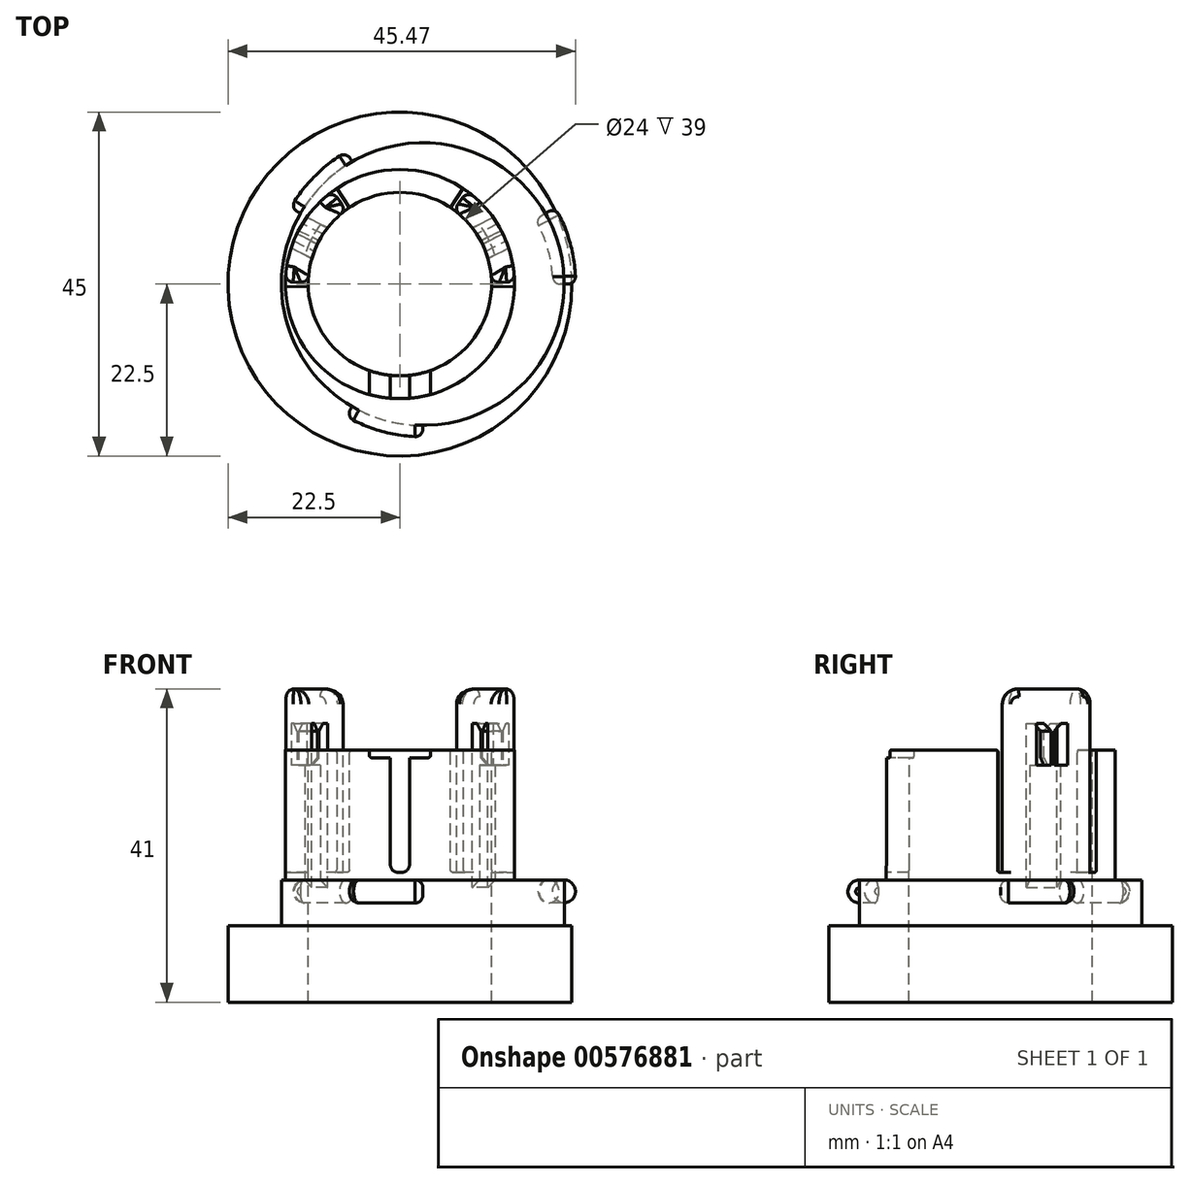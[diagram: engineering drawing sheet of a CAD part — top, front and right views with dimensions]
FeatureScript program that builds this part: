
annotation { "Feature Type Name" : "Feature", "Feature Type Description" : "" }
export const myFeature = defineFeature(function(context is Context, id is Id, definition is map)
    precondition{}
    {
        {
            var Q0;
            Q0=qCreatedBy(makeId("Top.planeOp"),FACE);
            var sketch = newSketch(context, id + "F0", { "sketchPlane" : qUnion([Q0])});
            skCircle(sketch, "E0", {"center": v(0, 0) * mm, "radius": 22.5 * mm});
            skCircle(sketch, "E1", {"center": v(0, 0) * mm, "radius": 12 * mm});
            skSolve(sketch);
        }
        {
            var Q0;
            Q0=makeQuery(id+"F0.imprint","IMPRINT",FACE,{"disambiguationData":[TD([[makeQuery(id+"F0.imprint","IMPRINT",EDGE,{"derivedFrom":sQuery(id+"F0.wireOp",EDGE,"E0")}),1.0]])]});
            extrude(context, id + "F1", {"entities" : qUnion([Q0]), "oppositeDirection" : true, "depth" : 5 * mm, "offsetDistance" : 25 * mm, "hasSecondDirection" : true, "secondDirectionOppositeDirection" : false, "secondDirectionDepth" : 5 * mm});
        }
        {
            var Q0;
            Q0=qCreatedBy(makeId("Top.planeOp"),FACE);
            var sketch = newSketch(context, id + "F2", { "sketchPlane" : qUnion([Q0])});
            skCircle(sketch, "E2", {"center": v(0, 0) * mm, "radius": 12 * mm});
            skCircle(sketch, "E3", {"center": v(3, 0) * mm, "radius": 18.5 * mm});
            skSolve(sketch);
        }
        {
            var Q0;
            Q0 = qSketchRegion(id + "F2", true);
            extrude(context, id + "F3", {"entities" : qUnion([Q0]), "operationType" : NewBodyOperationType.ADD, "depth" : 11 * mm, "offsetDistance" : 25 * mm});
        }
        {
            var Q0;
            Q0=qCreatedBy(makeId("Top.planeOp"),FACE);
            var sketch = newSketch(context, id + "F4", { "sketchPlane" : qUnion([Q0])});
            skCircle(sketch, "E4", {"center": v(0, 0) * mm, "radius": 12 * mm});
            skCircle(sketch, "E5", {"center": v(0, 0) * mm, "radius": 15 * mm});
            skSolve(sketch);
        }
        {
            var Q0;
            Q0 = qSketchRegion(id + "F4", true);
            extrude(context, id + "F5", {"entities" : qUnion([Q0]), "operationType" : NewBodyOperationType.ADD, "depth" : 28 * mm, "offsetDistance" : 25 * mm});
        }
        {
            var Q0;
            Q0=qCreatedBy(makeId("Front.planeOp"),FACE);
            var sketch = newSketch(context, id + "F6", { "sketchPlane" : qUnion([Q0])});
            skCircle(sketch, "E6", {"center": v(21.5, 9.5) * mm, "radius": 1.5 * mm});
            skLineSegment(sketch, "E7", {"start": v(3, -7.37) * mm, "end": v(3, 20.39) * mm});
            skSolve(sketch);
        }
        {
            var Q0;
            Q0=makeQuery(id+"F6.imprint","IMPRINT",FACE,{"disambiguationData":[TD([[makeQuery(id+"F6.imprint","IMPRINT",EDGE,{"derivedFrom":sQuery(id+"F6.wireOp",EDGE,"E6")}),1.0]])]});
            var Q1;
            Q1=sQuery(id+"F6.wireOp",EDGE,"E7");
            revolve(context, id + "F7", {"entities" : qUnion([Q0]), "axis" : qUnion([Q1]), "revolveType" : RevolveType.ONE_DIRECTION, "angle" : 30 * degree});
        }
        {
            var Q0;
            Q0 = qSketchRegion(id + "F6", true);
            var Q1;
            Q1=sQuery(id+"F6.wireOp",EDGE,"E7");
            revolve(context, id + "F8", {"operationType" : NewBodyOperationType.ADD, "entities" : qUnion([Q0]), "axis" : qUnion([Q1]), "revolveType" : RevolveType.TWO_DIRECTIONS, "angle" : 150 * degree, "angleBack" : 120 * degree});
        }
        {
            var Q0;
            Q0 = qSketchRegion(id + "F6", true);
            var Q1;
            Q1=sQuery(id+"F6.wireOp",EDGE,"E7");
            revolve(context, id + "F9", {"operationType" : NewBodyOperationType.ADD, "entities" : qUnion([Q0]), "axis" : qUnion([Q1]), "revolveType" : RevolveType.TWO_DIRECTIONS, "angle" : 270 * degree, "angleBack" : 240 * degree});
        }
        {
            var Q0;
            Q0=makeQuery(id+"F9.opRevolve","CAP_EDGE",EDGE,{"disambiguationData":[OSD([sQuery(id+"F6.wireOp",EDGE,"E6")])],"isStart":false});
            var Q1;
            Q1=makeQuery(id+"F9.opRevolve","CAP_EDGE",EDGE,{"disambiguationData":[OSD([sQuery(id+"F6.wireOp",EDGE,"E6")])],"isStart":true});
            var Q2;
            Q2=makeQuery(id+"F7.opRevolve","CAP_EDGE",EDGE,{"disambiguationData":[OSD([sQuery(id+"F6.wireOp",EDGE,"E6")])],"isStart":true});
            var Q3;
            Q3=makeQuery(id+"F7.opRevolve","CAP_EDGE",EDGE,{"disambiguationData":[OSD([sQuery(id+"F6.wireOp",EDGE,"E6")])],"isStart":false});
            var Q4;
            Q4=makeQuery(id+"F8.opRevolve","CAP_EDGE",EDGE,{"disambiguationData":[OSD([sQuery(id+"F6.wireOp",EDGE,"E6")])],"isStart":true});
            var Q5;
            Q5=makeQuery(id+"F8.opRevolve","CAP_EDGE",EDGE,{"disambiguationData":[OSD([sQuery(id+"F6.wireOp",EDGE,"E6")])],"isStart":false});
            fillet(context, id + "F10", {"entities" : qUnion([Q0, Q1, Q2, Q3, Q4, Q5]), "radius" : 1 * mm, "tangentPropagation" : true, "allowEdgeOverflow" : false});
        }
        {
            var Q0;
            Q0=qCreatedBy(makeId("Top.planeOp"),FACE);
            var sketch = newSketch(context, id + "F11", { "sketchPlane" : qUnion([Q0])});
            skLineSegment(sketch, "E8.bottom", {"start": v(-1.25, -10) * mm, "end": v(1.25, -10) * mm});
            skLineSegment(sketch, "E8.left", {"start": v(-1.25, -10) * mm, "end": v(-1.25, -14.95) * mm});
            skLineSegment(sketch, "E8.right", {"start": v(1.25, -10) * mm, "end": v(1.25, -14.95) * mm});
            skArc(sketch, "E9", {"start": v(-1.25, -14.95) * mm, "mid": v(0, -15) * mm, "end": v(1.25, -14.95) * mm});
            skLineSegment(sketch, "E10", {"start": v(0, 0) * mm, "end": v(-15, -0.4) * mm});
            skLineSegment(sketch, "E11", {"start": v(0, 0) * mm, "end": v(-8.28, 12.5) * mm});
            skLineSegment(sketch, "E12", {"start": v(0, 0) * mm, "end": v(8.28, 12.5) * mm});
            skLineSegment(sketch, "E13", {"start": v(0, 0) * mm, "end": v(15, -0.4) * mm});
            skArc(sketch, "E14.trimOffspring", {"start": v(-8.28, 12.5) * mm, "mid": v(-13.3, 6.93) * mm, "end": v(-15, -0.4) * mm});
            skArc(sketch, "E15.trimOffspring", {"start": v(15, -0.4) * mm, "mid": v(13.3, 6.93) * mm, "end": v(8.28, 12.5) * mm});
            skSolve(sketch);
        }
        {
            var Q0;
            Q0 = qSketchRegion(id + "F11", true);
            extrude(context, id + "F12", {"entities" : qUnion([Q0]), "operationType" : NewBodyOperationType.REMOVE, "depth" : 32 * mm, "offsetDistance" : 25 * mm, "hasSecondDirection" : true, "secondDirectionOppositeDirection" : false, "secondDirectionDepth" : 12 * mm});
        }
        {
            var Q0;
            Q0=makeQuery(id+"F12.boolean.opBoolean","COPY",EDGE,{"derivedFrom":makeQuery(id+"F12.opExtrude","CAP_EDGE",EDGE,{"disambiguationData":[OSD([sQuery(id+"F11.wireOp",EDGE,"E8.left")])],"isStart":true})});
            var Q1;
            Q1=makeQuery(id+"F12.boolean.opBoolean","COPY",EDGE,{"derivedFrom":makeQuery(id+"F12.opExtrude","CAP_EDGE",EDGE,{"disambiguationData":[OSD([sQuery(id+"F11.wireOp",EDGE,"E8.right")])],"isStart":true})});
            fillet(context, id + "F13", {"entities" : qUnion([Q0, Q1]), "radius" : 1 * mm, "tangentPropagation" : true, "allowEdgeOverflow" : false});
        }
        {
            var Q0;
            Q0=qCreatedBy(makeId("Top.planeOp"),FACE);
            var sketch = newSketch(context, id + "F14", { "sketchPlane" : qUnion([Q0])});
            skArc(sketch, "E16", {"start": v(-8.82, 12.14) * mm, "mid": v(-13.3, 6.93) * mm, "end": v(-15, 0.26) * mm});
            skArc(sketch, "E17", {"start": v(-7.05, 9.7) * mm, "mid": v(-10.64, 5.54) * mm, "end": v(-12, 0.2) * mm});
            skLineSegment(sketch, "E18", {"start": v(-12, 0.2) * mm, "end": v(-15, 0.26) * mm});
            skLineSegment(sketch, "E19", {"start": v(-7.05, 9.7) * mm, "end": v(-8.82, 12.14) * mm});
            skLineSegment(sketch, "E20", {"start": v(7.05, 9.7) * mm, "end": v(8.82, 12.14) * mm});
            skLineSegment(sketch, "E21", {"start": v(12, 0.2) * mm, "end": v(15, 0.26) * mm});
            skArc(sketch, "E22.trimOffspring", {"start": v(15, 0.26) * mm, "mid": v(13.3, 6.93) * mm, "end": v(8.82, 12.14) * mm});
            skArc(sketch, "E23.trimOffspring", {"start": v(12, 0.2) * mm, "mid": v(10.64, 5.54) * mm, "end": v(7.05, 9.7) * mm});
            skSolve(sketch);
        }
        {
            var Q0;
            Q0 = qSketchRegion(id + "F14", true);
            extrude(context, id + "F15", {"entities" : qUnion([Q0]), "operationType" : NewBodyOperationType.ADD, "depth" : 36 * mm, "offsetDistance" : 25 * mm, "hasSecondDirection" : true, "secondDirectionOppositeDirection" : false, "secondDirectionDepth" : 11 * mm});
        }
        {
            var Q0;
            Q0=makeQuery(id+"F15.opExtrude","SWEPT_EDGE",EDGE,{"disambiguationData":[OSD([sQuery(id+"F14.wireOp",EDGE,"E16"),sQuery(id+"F14.wireOp",EDGE,"E18")])]});
            var Q1;
            Q1=makeQuery(id+"F15.opExtrude","SWEPT_EDGE",EDGE,{"disambiguationData":[OSD([sQuery(id+"F14.wireOp",EDGE,"E16"),sQuery(id+"F14.wireOp",EDGE,"E19")])]});
            var Q2;
            Q2=makeQuery(id+"F15.opExtrude","SWEPT_EDGE",EDGE,{"disambiguationData":[OSD([sQuery(id+"F14.wireOp",EDGE,"E17"),sQuery(id+"F14.wireOp",EDGE,"E18")])]});
            var Q3;
            Q3=makeQuery(id+"F15.opExtrude","SWEPT_EDGE",EDGE,{"disambiguationData":[OSD([sQuery(id+"F14.wireOp",EDGE,"E17"),sQuery(id+"F14.wireOp",EDGE,"E19")])]});
            var Q4;
            Q4=makeQuery(id+"F15.opExtrude","CAP_EDGE",EDGE,{"disambiguationData":[OSD([sQuery(id+"F14.wireOp",EDGE,"E16")])],"isStart":false});
            var Q5;
            Q5=makeQuery(id+"F15.opExtrude","SWEPT_EDGE",EDGE,{"disambiguationData":[OSD([sQuery(id+"F14.wireOp",EDGE,"E20"),sQuery(id+"F14.wireOp",EDGE,"E23.trimOffspring")])]});
            var Q6;
            Q6=makeQuery(id+"F15.opExtrude","SWEPT_EDGE",EDGE,{"disambiguationData":[OSD([sQuery(id+"F14.wireOp",EDGE,"E21"),sQuery(id+"F14.wireOp",EDGE,"E23.trimOffspring")])]});
            var Q7;
            Q7=makeQuery(id+"F15.opExtrude","SWEPT_EDGE",EDGE,{"disambiguationData":[OSD([sQuery(id+"F14.wireOp",EDGE,"E21"),sQuery(id+"F14.wireOp",EDGE,"E22.trimOffspring")])]});
            var Q8;
            Q8=makeQuery(id+"F15.opExtrude","CAP_EDGE",EDGE,{"disambiguationData":[OSD([sQuery(id+"F14.wireOp",EDGE,"E22.trimOffspring")])],"isStart":false});
            var Q9;
            Q9=makeQuery(id+"F15.opExtrude","SWEPT_EDGE",EDGE,{"disambiguationData":[OSD([sQuery(id+"F14.wireOp",EDGE,"E20"),sQuery(id+"F14.wireOp",EDGE,"E22.trimOffspring")])]});
            fillet(context, id + "F16", {"entities" : qUnion([Q0, Q1, Q2, Q3, Q4, Q5, Q6, Q7, Q8, Q9]), "radius" : 1 * mm, "tangentPropagation" : true, "allowEdgeOverflow" : false});
        }
        {
            var Q0;
            Q0=makeQuery(id+"F15.opExtrude","CAP_EDGE",EDGE,{"disambiguationData":[OSD([sQuery(id+"F14.wireOp",EDGE,"E17")])],"isStart":false});
            var Q1;
            Q1=makeQuery(id+"F15.opExtrude","CAP_EDGE",EDGE,{"disambiguationData":[OSD([sQuery(id+"F14.wireOp",EDGE,"E23.trimOffspring")])],"isStart":false});
            var Q2;
            Q2=makeQuery(id+"F15.opExtrude","CAP_EDGE",EDGE,{"disambiguationData":[OSD([sQuery(id+"F14.wireOp",EDGE,"E20")])],"isStart":false});
            var Q3;
            Q3=makeQuery(id+"F15.opExtrude","CAP_EDGE",EDGE,{"disambiguationData":[OSD([sQuery(id+"F14.wireOp",EDGE,"E21")])],"isStart":false});
            var Q4;
            Q4=makeQuery(id+"F15.opExtrude","CAP_EDGE",EDGE,{"disambiguationData":[OSD([sQuery(id+"F14.wireOp",EDGE,"E19")])],"isStart":false});
            var Q5;
            Q5=makeQuery(id+"F15.opExtrude","CAP_EDGE",EDGE,{"disambiguationData":[OSD([sQuery(id+"F14.wireOp",EDGE,"E18")])],"isStart":false});
            fillet(context, id + "F17", {"entities" : qUnion([Q0, Q1, Q2, Q3, Q4, Q5]), "radius" : 2 * mm, "tangentPropagation" : true, "allowEdgeOverflow" : false});
        }
        {
            var Q0;
            Q0=qCreatedBy(makeId("Top.planeOp"),FACE);
            var sketch = newSketch(context, id + "F18", { "sketchPlane" : qUnion([Q0])});
            skLineSegment(sketch, "E24", {"start": v(-5.22, 5.18) * mm, "end": v(-14.13, 9.72) * mm});
            skLineSegment(sketch, "E25", {"start": v(-7.26, 1.17) * mm, "end": v(-16.17, 5.71) * mm});
            skLineSegment(sketch, "E26", {"start": v(-16.17, 5.71) * mm, "end": v(-15.26, 7.5) * mm});
            skLineSegment(sketch, "E27", {"start": v(-7.26, 1.17) * mm, "end": v(-6.35, 2.96) * mm});
            skLineSegment(sketch, "E28.MirrorCS", {"start": v(7.26, 1.17) * mm, "end": v(6.35, 2.96) * mm});
            skLineSegment(sketch, "E29.MirrorCS", {"start": v(5.22, 5.18) * mm, "end": v(14.13, 9.72) * mm});
            skLineSegment(sketch, "E30.MirrorCS", {"start": v(16.17, 5.71) * mm, "end": v(15.26, 7.5) * mm});
            skLineSegment(sketch, "E31.MirrorCS", {"start": v(7.26, 1.17) * mm, "end": v(16.17, 5.71) * mm});
            skLineSegment(sketch, "E32", {"start": v(-15.03, 7.94) * mm, "end": v(-6.12, 3.4) * mm});
            skLineSegment(sketch, "E33", {"start": v(-6.35, 2.96) * mm, "end": v(-15.26, 7.5) * mm});
            skLineSegment(sketch, "E34", {"start": v(6.12, 3.4) * mm, "end": v(15.03, 7.94) * mm});
            skLineSegment(sketch, "E35", {"start": v(6.35, 2.96) * mm, "end": v(15.26, 7.5) * mm});
            skLineSegment(sketch, "E36.trimOffspring", {"start": v(-15.03, 7.94) * mm, "end": v(-14.13, 9.72) * mm});
            skLineSegment(sketch, "E37.trimOffspring", {"start": v(-6.12, 3.4) * mm, "end": v(-5.22, 5.18) * mm});
            skLineSegment(sketch, "E38.trimOffspring", {"start": v(6.12, 3.4) * mm, "end": v(5.22, 5.18) * mm});
            skLineSegment(sketch, "E39.trimOffspring", {"start": v(15.03, 7.94) * mm, "end": v(14.13, 9.72) * mm});
            skSolve(sketch);
        }
        {
            var Q0;
            Q0 = qSketchRegion(id + "F18", true);
            extrude(context, id + "F19", {"entities" : qUnion([Q0]), "operationType" : NewBodyOperationType.REMOVE, "depth" : 31.5 * mm, "offsetDistance" : 25 * mm, "hasSecondDirection" : true, "secondDirectionOppositeDirection" : false, "secondDirectionDepth" : 26 * mm});
        }
        {
            var Q0;
            Q0=qCreatedBy(makeId("Top.planeOp"),FACE);
            var sketch = newSketch(context, id + "F20", { "sketchPlane" : qUnion([Q0])});
            skLineSegment(sketch, "E40.bottom", {"start": v(-4, -8) * mm, "end": v(4, -8) * mm});
            skLineSegment(sketch, "E40.top", {"start": v(-4, -16) * mm, "end": v(4, -16) * mm});
            skLineSegment(sketch, "E40.left", {"start": v(-4, -8) * mm, "end": v(-4, -16) * mm});
            skLineSegment(sketch, "E40.right", {"start": v(4, -8) * mm, "end": v(4, -16) * mm});
            skSolve(sketch);
        }
        {
            var Q0;
            Q0 = qSketchRegion(id + "F20", true);
            extrude(context, id + "F21", {"entities" : qUnion([Q0]), "operationType" : NewBodyOperationType.REMOVE, "depth" : 30 * mm, "offsetDistance" : 25 * mm, "hasSecondDirection" : true, "secondDirectionOppositeDirection" : false, "secondDirectionDepth" : 27 * mm});
        }
        {
            var Q0;
            Q0=qCreatedBy(makeId("Top.planeOp"),FACE);
            var sketch = newSketch(context, id + "F22", { "sketchPlane" : qUnion([Q0])});
            skArc(sketch, "E41", {"start": v(-10.39, 7.82) * mm, "mid": v(-11.58, 5.9) * mm, "end": v(-12.43, 3.8) * mm});
            skArc(sketch, "E42", {"start": v(-9.48, 7.36) * mm, "mid": v(-10.7, 5.45) * mm, "end": v(-11.52, 3.35) * mm});
            skLineSegment(sketch, "E43", {"start": v(-9.48, 7.36) * mm, "end": v(-10.39, 7.82) * mm});
            skLineSegment(sketch, "E44", {"start": v(-11.52, 3.35) * mm, "end": v(-12.43, 3.8) * mm});
            skArc(sketch, "E45.MirrorCS", {"start": v(9.48, 7.36) * mm, "mid": v(10.7, 5.45) * mm, "end": v(11.52, 3.35) * mm});
            skLineSegment(sketch, "E46.MirrorCS", {"start": v(9.48, 7.36) * mm, "end": v(10.39, 7.82) * mm});
            skArc(sketch, "E47.MirrorCS", {"start": v(10.39, 7.82) * mm, "mid": v(11.58, 5.9) * mm, "end": v(12.43, 3.8) * mm});
            skLineSegment(sketch, "E48.MirrorCS", {"start": v(11.52, 3.35) * mm, "end": v(12.43, 3.8) * mm});
            skSolve(sketch);
        }
        {
            var Q0;
            Q0 = qSketchRegion(id + "F22", true);
            extrude(context, id + "F23", {"entities" : qUnion([Q0]), "operationType" : NewBodyOperationType.REMOVE, "depth" : 27 * mm, "offsetDistance" : 25 * mm, "hasSecondDirection" : true, "secondDirectionOppositeDirection" : false, "secondDirectionDepth" : 10 * mm});
        }
        {
            var Q0;
            Q0=makeQuery(id+"F21.boolean.opBoolean","COPY",EDGE,{"derivedFrom":makeQuery(id+"F21.opExtrude","CAP_EDGE",EDGE,{"disambiguationData":[OSD([sQuery(id+"F20.wireOp",EDGE,"E40.left")])],"isStart":true})});
            var Q1;
            {var subQ0=sQuery(id+"F4.wireOp",EDGE,"E5");var subQ1=sQuery(id+"F4.wireOp",EDGE,"E4");Q1=makeQuery(id+"F21.boolean.opBoolean","INTERSECT",EDGE,{"derivedFrom":[makeQuery(id+"F12.boolean.opBoolean","SPLIT",FACE,{"disambiguationData":[TD([makeQuery(id+"F12.opExtrude","SWEPT_FACE",FACE,{"disambiguationData":[OSD([sQuery(id+"F11.wireOp",EDGE,"E8.right")])]})])],"derivedFrom":makeQuery(id+"F5.opExtrude","CAP_FACE",FACE,{"disambiguationData":[OSD([subQ1,subQ0])],"isStart":false})}),makeQuery(id+"F21.opExtrude","SWEPT_FACE",FACE,{"disambiguationData":[OSD([sQuery(id+"F20.wireOp",EDGE,"E40.right")])]})]});}
            var Q2;
            Q2=makeQuery(id+"F21.boolean.opBoolean","COPY",EDGE,{"derivedFrom":makeQuery(id+"F21.opExtrude","CAP_EDGE",EDGE,{"disambiguationData":[OSD([sQuery(id+"F20.wireOp",EDGE,"E40.right")])],"isStart":true})});
            var Q3;
            {var subQ0=sQuery(id+"F4.wireOp",EDGE,"E5");var subQ1=sQuery(id+"F4.wireOp",EDGE,"E4");Q3=makeQuery(id+"F21.boolean.opBoolean","INTERSECT",EDGE,{"derivedFrom":[makeQuery(id+"F12.boolean.opBoolean","SPLIT",FACE,{"disambiguationData":[TD([makeQuery(id+"F12.opExtrude","SWEPT_FACE",FACE,{"disambiguationData":[OSD([sQuery(id+"F11.wireOp",EDGE,"E8.left")])]})])],"derivedFrom":makeQuery(id+"F5.opExtrude","CAP_FACE",FACE,{"disambiguationData":[OSD([subQ1,subQ0])],"isStart":false})}),makeQuery(id+"F21.opExtrude","SWEPT_FACE",FACE,{"disambiguationData":[OSD([sQuery(id+"F20.wireOp",EDGE,"E40.left")])]})]});}
            var Q4;
            Q4=makeQuery(id+"F12.boolean.opBoolean","COPY",EDGE,{"derivedFrom":makeQuery(id+"F12.opExtrude","CAP_EDGE",EDGE,{"disambiguationData":[OSD([sQuery(id+"F11.wireOp",EDGE,"E13")])],"isStart":true})});
            var Q5;
            Q5=makeQuery(id+"F12.boolean.opBoolean","INTERSECT",EDGE,{"derivedFrom":[makeQuery(id+"F5.opExtrude","CAP_FACE",FACE,{"disambiguationData":[OSD([sQuery(id+"F4.wireOp",EDGE,"E4"),sQuery(id+"F4.wireOp",EDGE,"E5")])],"isStart":false}),makeQuery(id+"F12.opExtrude","SWEPT_FACE",FACE,{"disambiguationData":[OSD([sQuery(id+"F11.wireOp",EDGE,"E13")])]})]});
            var Q6;
            Q6=makeQuery(id+"F12.boolean.opBoolean","COPY",EDGE,{"derivedFrom":makeQuery(id+"F12.opExtrude","CAP_EDGE",EDGE,{"disambiguationData":[OSD([sQuery(id+"F11.wireOp",EDGE,"E12")])],"isStart":true})});
            var Q7;
            Q7=makeQuery(id+"F12.boolean.opBoolean","INTERSECT",EDGE,{"derivedFrom":[makeQuery(id+"F5.opExtrude","CAP_FACE",FACE,{"disambiguationData":[OSD([sQuery(id+"F4.wireOp",EDGE,"E4"),sQuery(id+"F4.wireOp",EDGE,"E5")])],"isStart":false}),makeQuery(id+"F12.opExtrude","SWEPT_FACE",FACE,{"disambiguationData":[OSD([sQuery(id+"F11.wireOp",EDGE,"E12")])]})]});
            var Q8;
            Q8=makeQuery(id+"F12.boolean.opBoolean","INTERSECT",EDGE,{"derivedFrom":[makeQuery(id+"F5.opExtrude","CAP_FACE",FACE,{"disambiguationData":[OSD([sQuery(id+"F4.wireOp",EDGE,"E4"),sQuery(id+"F4.wireOp",EDGE,"E5")])],"isStart":false}),makeQuery(id+"F12.opExtrude","SWEPT_FACE",FACE,{"disambiguationData":[OSD([sQuery(id+"F11.wireOp",EDGE,"E10")])]})]});
            var Q9;
            Q9=makeQuery(id+"F12.boolean.opBoolean","INTERSECT",EDGE,{"derivedFrom":[makeQuery(id+"F5.opExtrude","CAP_FACE",FACE,{"disambiguationData":[OSD([sQuery(id+"F4.wireOp",EDGE,"E4"),sQuery(id+"F4.wireOp",EDGE,"E5")])],"isStart":false}),makeQuery(id+"F12.opExtrude","SWEPT_FACE",FACE,{"disambiguationData":[OSD([sQuery(id+"F11.wireOp",EDGE,"E11")])]})]});
            var Q10;
            Q10=makeQuery(id+"F12.boolean.opBoolean","COPY",EDGE,{"derivedFrom":makeQuery(id+"F12.opExtrude","CAP_EDGE",EDGE,{"disambiguationData":[OSD([sQuery(id+"F11.wireOp",EDGE,"E11")])],"isStart":true})});
            var Q11;
            Q11=makeQuery(id+"F12.boolean.opBoolean","COPY",EDGE,{"derivedFrom":makeQuery(id+"F12.opExtrude","CAP_EDGE",EDGE,{"disambiguationData":[OSD([sQuery(id+"F11.wireOp",EDGE,"E10")])],"isStart":true})});
            fillet(context, id + "F24", {"entities" : qUnion([Q0, Q1, Q2, Q3, Q4, Q5, Q6, Q7, Q8, Q9, Q10, Q11]), "radius" : 0.3 * mm, "tangentPropagation" : true, "allowEdgeOverflow" : false});
        }
        {
            var Q0;
            Q0=makeQuery(id+"F19.boolean.opBoolean","COPY",EDGE,{"derivedFrom":makeQuery(id+"F19.opExtrude","CAP_EDGE",EDGE,{"disambiguationData":[OSD([sQuery(id+"F18.wireOp",EDGE,"E33")])],"isStart":false})});
            var Q1;
            Q1=makeQuery(id+"F19.boolean.opBoolean","COPY",EDGE,{"derivedFrom":makeQuery(id+"F19.opExtrude","CAP_EDGE",EDGE,{"disambiguationData":[OSD([sQuery(id+"F18.wireOp",EDGE,"E32")])],"isStart":false})});
            var Q2;
            Q2=makeQuery(id+"F19.boolean.opBoolean","COPY",EDGE,{"derivedFrom":makeQuery(id+"F19.opExtrude","CAP_EDGE",EDGE,{"disambiguationData":[OSD([sQuery(id+"F18.wireOp",EDGE,"E34")])],"isStart":false})});
            var Q3;
            Q3=makeQuery(id+"F19.boolean.opBoolean","COPY",EDGE,{"derivedFrom":makeQuery(id+"F19.opExtrude","CAP_EDGE",EDGE,{"disambiguationData":[OSD([sQuery(id+"F18.wireOp",EDGE,"E35")])],"isStart":false})});
            chamfer(context, id + "F25", {"entities" : qUnion([Q0, Q1, Q2, Q3]), "width" : 1 * mm, "tangentPropagation" : true});
        }
        {
            var Q0;
            Q0=makeQuery(id+"F23.boolean.opBoolean","COPY",EDGE,{"derivedFrom":makeQuery(id+"F23.opExtrude","CAP_EDGE",EDGE,{"disambiguationData":[OSD([sQuery(id+"F22.wireOp",EDGE,"E41")])],"isStart":false})});
            var Q1;
            Q1=makeQuery(id+"F23.boolean.opBoolean","COPY",EDGE,{"derivedFrom":makeQuery(id+"F23.opExtrude","CAP_EDGE",EDGE,{"disambiguationData":[OSD([sQuery(id+"F22.wireOp",EDGE,"E47.MirrorCS")])],"isStart":false})});
            var Q2;
            Q2=makeQuery(id+"F23.boolean.opBoolean","COPY",EDGE,{"derivedFrom":makeQuery(id+"F23.opExtrude","CAP_EDGE",EDGE,{"disambiguationData":[OSD([sQuery(id+"F22.wireOp",EDGE,"E41")])],"isStart":true})});
            var Q3;
            Q3=makeQuery(id+"F23.boolean.opBoolean","COPY",EDGE,{"derivedFrom":makeQuery(id+"F23.opExtrude","CAP_EDGE",EDGE,{"disambiguationData":[OSD([sQuery(id+"F22.wireOp",EDGE,"E47.MirrorCS")])],"isStart":true})});
            chamfer(context, id + "F26", {"entities" : qUnion([Q0, Q1, Q2, Q3]), "width" : 1 * mm, "tangentPropagation" : true});
        }
    });
